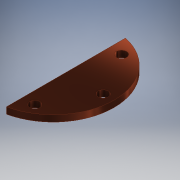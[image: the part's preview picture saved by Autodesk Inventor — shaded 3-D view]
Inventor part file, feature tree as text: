
AUTODESK INVENTOR PART (.ipt)
format: ipt  version: 2017.3 (Build 213256000, 256)  size: 182,272 bytes
history: native  units: mm
features: extrude x2, move_body x2, sketch x2
ambient origin geometry x8: Origin, YZ Plane, XZ Plane, XY Plane, X Axis, Y Axis, Z Axis, Center Point
bodies: Solid1 (feature_tree)
feature tree (6):
  extrude  "Extrusion1"  Depth=1.0mm TaperAngle=0.0deg
  extrude  "Extrusion2"  Depth=10.0mm
  move_body  "Move Body1"
  move_body  "Move Body2"
  sketch  "Sketch1"  dims[d0=19.0mm d1=1.0mm d2=0.0mm]
  sketch  "Sketch2"  dims[d4=1.6mm d8=1.6mm d9=1.6mm d11=14.0mm d12=1.0mm d13=0.0mm d14=90.0deg d15=10.0mm d16=0.0mm d17=0.0mm]
